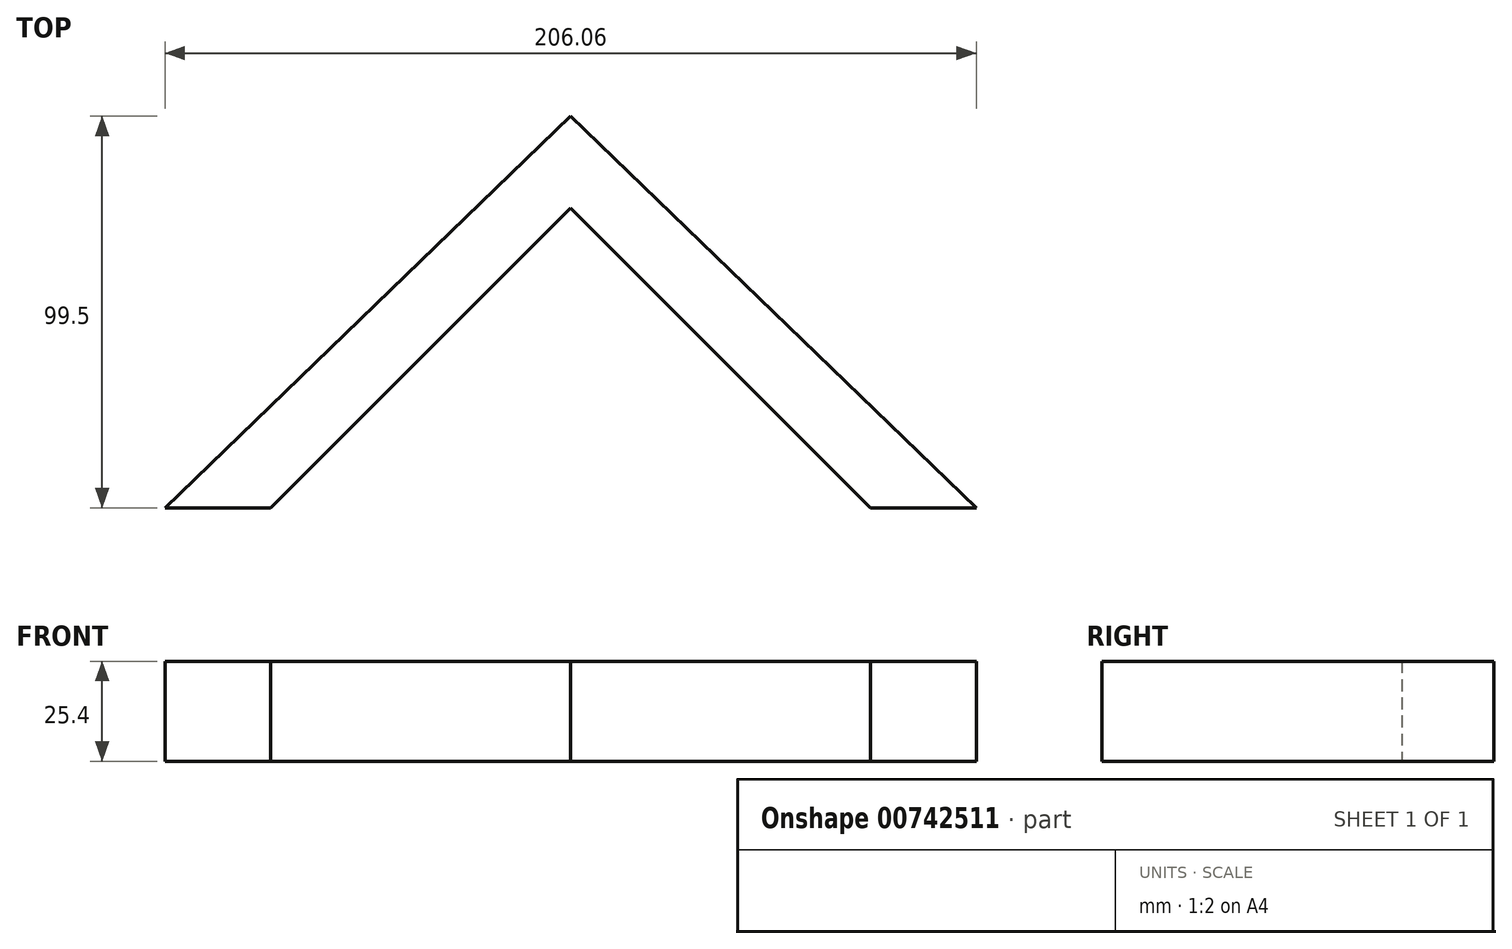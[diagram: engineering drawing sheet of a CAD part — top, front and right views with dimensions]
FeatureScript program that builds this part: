
annotation { "Feature Type Name" : "Feature", "Feature Type Description" : "" }
export const myFeature = defineFeature(function(context is Context, id is Id, definition is map)
    precondition{}
    {
        {
            var Q0;
            Q0=qCreatedBy(makeId("Top.planeOp"),FACE);
            var sketch = newSketch(context, id + "F0", { "sketchPlane" : qUnion([Q0])});
            skLineSegment(sketch, "E0", {"start": v(-76.2, 0) * mm, "end": v(0, 76.2) * mm});
            skLineSegment(sketch, "E1", {"start": v(0, 76.2) * mm, "end": v(76.2, 0) * mm});
            skLineSegment(sketch, "E2", {"start": v(76.2, 0) * mm, "end": v(103.03, 0) * mm});
            skLineSegment(sketch, "E3", {"start": v(103.03, 0) * mm, "end": v(0, 99.5) * mm});
            skLineSegment(sketch, "E4", {"start": v(0, 99.5) * mm, "end": v(-103.03, 0) * mm});
            skLineSegment(sketch, "E5", {"start": v(-103.03, 0) * mm, "end": v(-76.2, 0) * mm});
            skSolve(sketch);
        }
        {
            var Q0;
            Q0 = qSketchRegion(id + "F0", true);
            extrude(context, id + "F1", {"entities" : qUnion([Q0]), "depth" : 25.4 * mm, "offsetDistance" : 25.4 * mm});
        }
        {
            var Q0;
            Q0=makeQuery(id+"F1.opExtrude","SWEPT_FACE",FACE,{"disambiguationData":[OSD([sQuery(id+"F0.wireOp",EDGE,"E2")])]});
            var sketch = newSketch(context, id + "F2", { "sketchPlane" : qUnion([Q0])});
            skPoint(sketch, "E6.0", {"position": v(-103.03, 25.4) * mm});
            skPoint(sketch, "E6.1", {"position": v(103.03, 25.4) * mm});
            skLineSegment(sketch, "E7", {"start": v(103.03, 25.4) * mm, "end": v(-103.03, 25.4) * mm, "construction": true});
            skSolve(sketch);
        }
    });
